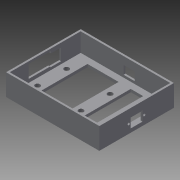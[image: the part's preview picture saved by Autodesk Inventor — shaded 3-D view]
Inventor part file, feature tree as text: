
AUTODESK INVENTOR PART (.ipt)
format: ipt  version: 2016 (Build 200138000, 138)  size: 226,304 bytes
history: native  units: mm
features: sketch x10, extrude x8, hole x4
ambient origin geometry x8: Origin, YZ Plane, XZ Plane, XY Plane, X Axis, Y Axis, Z Axis, Center Point
bodies: Solid1 (feature_tree)
feature tree (22):
  extrude  "Extrusion1"  Depth=120.0mm
  extrude  "Extrusion2"  Depth=3.0mm
  sketch  "Sketch3"  dims[d5=3.0mm d6=3.0mm]
  extrude  "Extrusion4"  Depth=3.0mm
  extrude  "Extrusion5"  Depth=30.0mm TaperAngle=0.0deg
  extrude  "Extrusion6"  Depth=12.5mm
  extrude  "Extrusion7"  Depth=4.0mm
  hole  "Hole3"  [1 undecoded]
  hole  "Hole5"  [1 undecoded]
  extrude  "Extrusion8"  Depth=34.5mm
  extrude  "Extrusion9"  Depth=6.85mm
  sketch  "Sketch1"  dims[d0=150.0mm d1=120.0mm]
  sketch  "Sketch2"  dims[d2=4.5mm d3=0.0mm d4=3.0mm]
  sketch  "Sketch5"  dims[d7=3.0mm d8=30.0mm d9=0.0mm]
  sketch  "Sketch6"  dims[d14=12.5mm d15=12.5mm]
  sketch  "Sketch7"  dims[d16=4.0mm d20=11.05mm]
  sketch  "Sketch8"  dims[d21=69.9mm d22=23.375mm]
  sketch  "Sketch10"  dims[d23=23.375mm d24=8.0mm]
  hole  "Hole2"  [1 undecoded]
  sketch  "Sketch11"  dims[d25=28.0mm d26=0.0mm d27=34.5mm]
  hole  "Hole4"  [1 undecoded]
  sketch  "Sketch12"  dims[d28=68.0mm d29=6.85mm d30=8.65mm d31=10.0mm d32=0.0mm d33=10.0mm d34=3.5mm d35=33.25mm d36=69.25mm d37=5.0mm d38=0.0mm d39=12.5mm d40=8.5mm d41=72.0mm d42=90.0mm d43=5.0mm d44=0.0mm d52=2.459mm d53=6.9mm d54=4.0mm d55=2.0mm d56=90.0deg d57=8.4mm d58=120.0deg d59=2.459mm d60=6.9mm d61=4.0mm d62=2.0mm d63=90.0deg d64=8.4mm d65=120.0deg d66=19.0mm d67=16.0mm d68=10.0mm d69=0.0mm d71=15.598mm d72=30.95mm d73=94.0mm d74=50.0mm d75=94.0mm d76=20.0mm d77=12.698mm d78=94.0mm d79=11.0mm d80=10.0mm d81=0.0mm]
note: 4 required parameter values undecoded (feature->parameter linkage not recoverable at this tier; creation-order binding heuristic only, values carry confidence <= 0.55)
